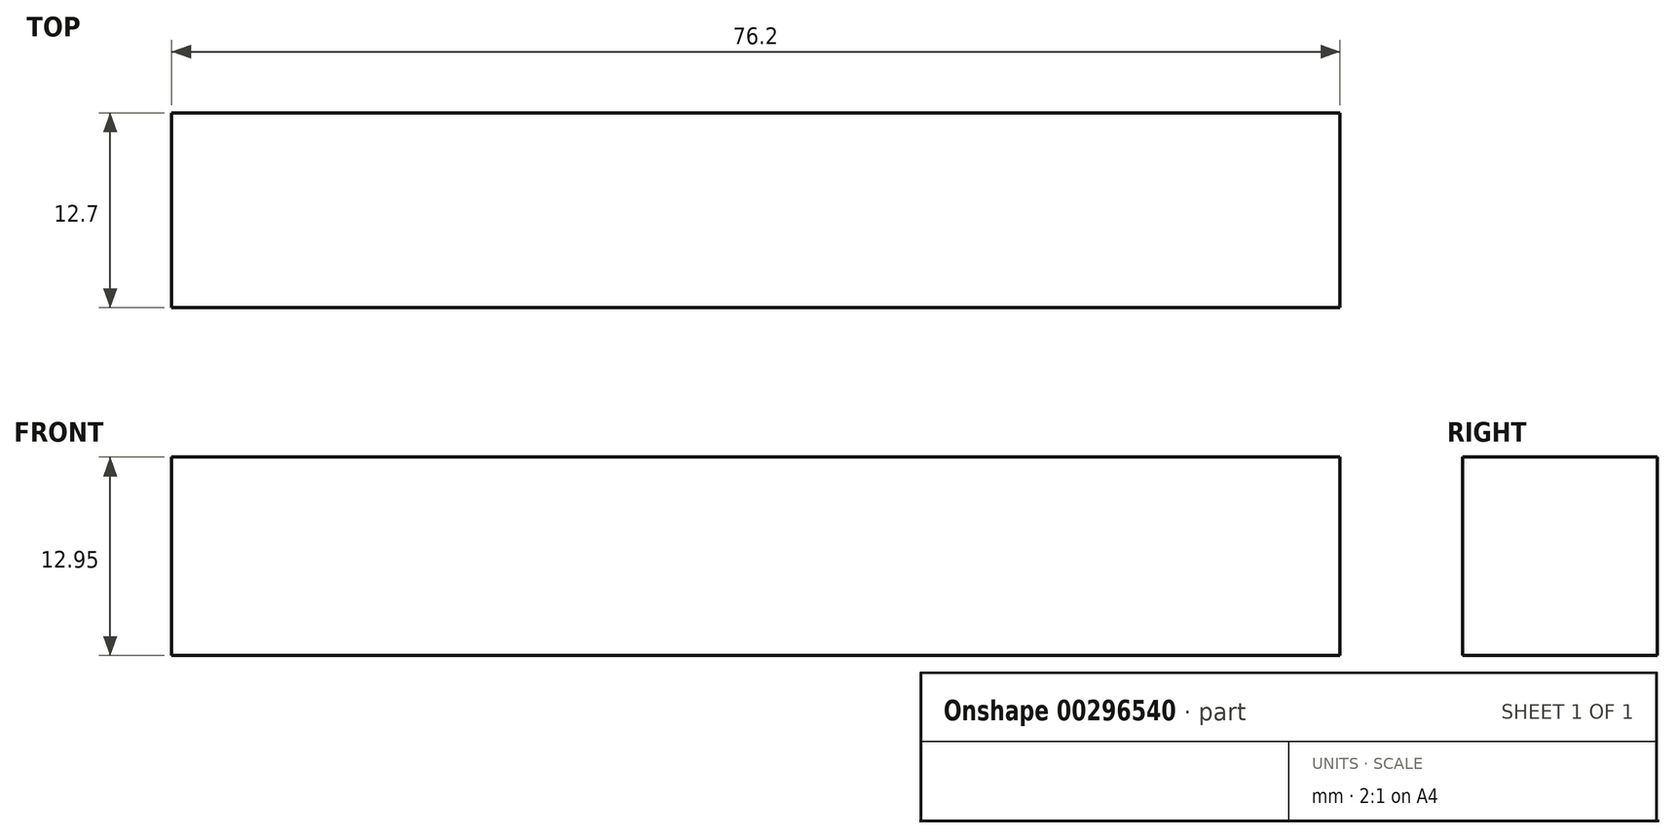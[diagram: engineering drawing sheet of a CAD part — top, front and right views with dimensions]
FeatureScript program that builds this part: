
annotation { "Feature Type Name" : "Feature", "Feature Type Description" : "" }
export const myFeature = defineFeature(function(context is Context, id is Id, definition is map)
    precondition{}
    {
        {
            var Q0;
            Q0=qCreatedBy(makeId("Front.planeOp"),FACE);
            var sketch = newSketch(context, id + "F0", { "sketchPlane" : qUnion([Q0])});
            skLineSegment(sketch, "E0.bottom", {"start": v(0, 0) * mm, "end": v(-76.2, 0) * mm});
            skLineSegment(sketch, "E0.top", {"start": v(0, 12.95) * mm, "end": v(-76.2, 12.95) * mm});
            skLineSegment(sketch, "E0.left", {"start": v(0, 0) * mm, "end": v(0, 12.95) * mm});
            skLineSegment(sketch, "E0.right", {"start": v(-76.2, 0) * mm, "end": v(-76.2, 12.95) * mm});
            skSolve(sketch);
        }
        {
            var Q0;
            Q0=makeQuery(id+"F0.imprint","IMPRINT",FACE,{"disambiguationData":[TD([[makeQuery(id+"F0.imprint","IMPRINT",EDGE,{"derivedFrom":sQuery(id+"F0.wireOp",EDGE,"E0.bottom")}),-1.0]])]});
            extrude(context, id + "F1", {"entities" : qUnion([Q0]), "depth" : 12.7 * mm});
        }
    });
